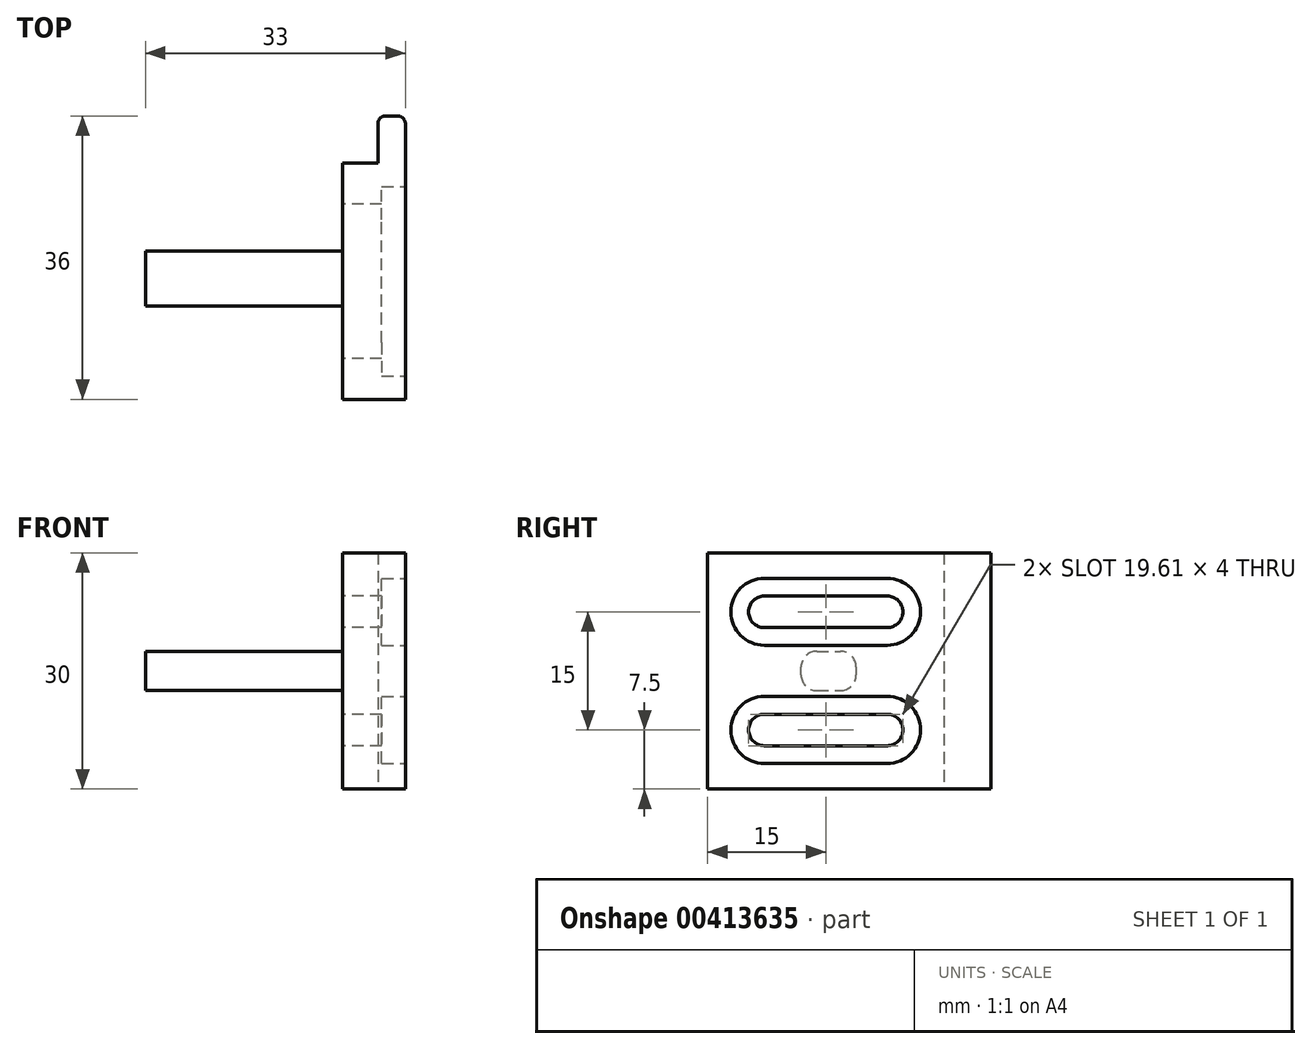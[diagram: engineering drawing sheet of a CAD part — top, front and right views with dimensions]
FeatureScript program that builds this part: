
annotation { "Feature Type Name" : "Feature", "Feature Type Description" : "" }
export const myFeature = defineFeature(function(context is Context, id is Id, definition is map)
    precondition{}
    {
        {
            var Q0;
            Q0=qCreatedBy(makeId("Top.planeOp"),FACE);
            var sketch = newSketch(context, id + "F0", { "sketchPlane" : qUnion([Q0])});
            skLineSegment(sketch, "E0", {"start": v(8, 36) * mm, "end": v(4.5, 36) * mm});
            skLineSegment(sketch, "E1", {"start": v(4.5, 36) * mm, "end": v(4.5, 30) * mm});
            skLineSegment(sketch, "E2", {"start": v(4.5, 30) * mm, "end": v(0, 30) * mm});
            skLineSegment(sketch, "E3", {"start": v(0, 30) * mm, "end": v(0, 0) * mm});
            skLineSegment(sketch, "E4", {"start": v(0, 0) * mm, "end": v(8, 0) * mm});
            skLineSegment(sketch, "E5", {"start": v(8, 0) * mm, "end": v(8, 36) * mm});
            skSolve(sketch);
        }
        {
            var Q0;
            Q0=qSketchRegion(id+"F0",true);
            extrude(context, id + "F1", {"entities" : qUnion([Q0]), "depth" : 30 * mm});
        }
        {
            var Q0;
            Q0=makeQuery(id+"F1.opExtrude","SWEPT_FACE",FACE,{"disambiguationData":[OSD([sQuery(id+"F0.wireOp",EDGE,"E3")])]});
            var sketch = newSketch(context, id + "F2", { "sketchPlane" : qUnion([Q0])});
            skLineSegment(sketch, "E6", {"start": v(-30, 15) * mm, "end": v(0, 15) * mm, "construction": true});
            skLineSegment(sketch, "E7", {"start": v(-7.2, 0) * mm, "end": v(-7.2, 30) * mm, "construction": true});
            skCircle(sketch, "E8", {"center": v(-7.2, 22.5) * mm, "radius": 2 * mm});
            skCircle(sketch, "E9.MirrorC", {"center": v(-7.2, 7.5) * mm, "radius": 2 * mm});
            skLineSegment(sketch, "E10", {"start": v(-15, 30) * mm, "end": v(-15, 0) * mm, "construction": true});
            skLineSegment(sketch, "E11", {"start": v(-7.2, 24.5) * mm, "end": v(-15, 24.5) * mm});
            skLineSegment(sketch, "E12", {"start": v(-7.2, 20.5) * mm, "end": v(-15, 20.5) * mm});
            skLineSegment(sketch, "E13.MirrorCS", {"start": v(-7.2, 5.5) * mm, "end": v(-15, 5.5) * mm});
            skLineSegment(sketch, "E14.MirrorCS", {"start": v(-7.2, 9.5) * mm, "end": v(-15, 9.5) * mm});
            skLineSegment(sketch, "E15.MirrorCS", {"start": v(-22.8, 24.5) * mm, "end": v(-15, 24.5) * mm});
            skLineSegment(sketch, "E16.MirrorCS", {"start": v(-22.8, 20.5) * mm, "end": v(-15, 20.5) * mm});
            skCircle(sketch, "E17.MirrorC", {"center": v(-22.8, 22.5) * mm, "radius": 2 * mm});
            skLineSegment(sketch, "E18.MirrorCS", {"start": v(-22.8, 5.5) * mm, "end": v(-15, 5.5) * mm});
            skLineSegment(sketch, "E19.MirrorCS", {"start": v(-22.8, 9.5) * mm, "end": v(-15, 9.5) * mm});
            skCircle(sketch, "E20.MirrorC", {"center": v(-22.8, 7.5) * mm, "radius": 2 * mm});
            skSolve(sketch);
        }
        {
            var Q0;
            Q0 = qSketchRegion(id + "F2", true);
            var Q1;
            Q1=sQuery(id+"F2.wireOp",EDGE,"E6");
            var Q2;
            Q2=sQuery(id+"F2.wireOp",EDGE,"E7");
            var Q3;
            Q3=sQuery(id+"F2.wireOp",EDGE,"Hv4J3IM8-VowD-CxZo-AhSj-27J0OBbzQMSq");
            var Q4;
            Q4=sQuery(id+"F2.wireOp",EDGE,"gJ8dOzfd-5YLx-k0AR-j59Q-bYQyRviPl2UG");
            extrude(context, id + "F3", {"entities" : qUnion([Q0]), "operationType" : NewBodyOperationType.REMOVE, "surfaceEntities" : qUnion([Q1, Q2, Q3, Q4]), "endBound" : BoundingType.THROUGH_ALL, "oppositeDirection" : true, "depth" : 25 * mm});
        }
        {
            var Q0;
            Q0=makeQuery(id+"F1.opExtrude","SWEPT_EDGE",EDGE,{"disambiguationData":[OSD([sQuery(id+"F0.wireOp",EDGE,"E0"),sQuery(id+"F0.wireOp",EDGE,"E1")])]});
            var Q1;
            Q1=makeQuery(id+"F1.opExtrude","SWEPT_EDGE",EDGE,{"disambiguationData":[OSD([sQuery(id+"F0.wireOp",EDGE,"E0"),sQuery(id+"F0.wireOp",EDGE,"E5")])]});
            fillet(context, id + "F4", {"entities" : qUnion([Q0, Q1]), "radius" : 1 * mm, "tangentPropagation" : true, "allowEdgeOverflow" : false});
        }
        {
            var Q0;
            Q0=makeQuery(id+"F1.opExtrude","SWEPT_FACE",FACE,{"disambiguationData":[OSD([sQuery(id+"F0.wireOp",EDGE,"E5")])]});
            var sketch = newSketch(context, id + "F5", { "sketchPlane" : qUnion([Q0])});
            skCircle(sketch, "E21", {"center": v(7.2, 22.5) * mm, "radius": 4.25 * mm});
            skCircle(sketch, "E22", {"center": v(7.2, 7.5) * mm, "radius": 4.25 * mm});
            skCircle(sketch, "E23", {"center": v(22.8, 22.5) * mm, "radius": 4.25 * mm});
            skCircle(sketch, "E24", {"center": v(22.8, 7.5) * mm, "radius": 4.25 * mm});
            skLineSegment(sketch, "E25", {"start": v(7.2, 26.75) * mm, "end": v(22.8, 26.75) * mm});
            skLineSegment(sketch, "E26", {"start": v(7.2, 18.25) * mm, "end": v(22.8, 18.25) * mm});
            skLineSegment(sketch, "E27", {"start": v(7.2, 11.75) * mm, "end": v(22.8, 11.75) * mm});
            skLineSegment(sketch, "E28", {"start": v(7.2, 3.25) * mm, "end": v(22.8, 3.25) * mm});
            skSolve(sketch);
        }
        {
            var Q0;
            Q0=qSketchRegion(id+"F5",true);
            extrude(context, id + "F6", {"entities" : qUnion([Q0]), "operationType" : NewBodyOperationType.REMOVE, "oppositeDirection" : true, "depth" : 3 * mm});
        }
        {
            var Q0;
            Q0=makeQuery(id+"F1.opExtrude","SWEPT_FACE",FACE,{"disambiguationData":[OSD([sQuery(id+"F0.wireOp",EDGE,"E3")])]});
            var sketch = newSketch(context, id + "F7", { "sketchPlane" : qUnion([Q0])});
            skLineSegment(sketch, "E29.bottom", {"start": v(-11.87, 12.5) * mm, "end": v(-18.85, 12.5) * mm});
            skLineSegment(sketch, "E29.left", {"start": v(-11.87, 12.5) * mm, "end": v(-11.87, 15) * mm});
            skLineSegment(sketch, "E29.right", {"start": v(-18.85, 12.5) * mm, "end": v(-18.85, 15) * mm});
            skLineSegment(sketch, "E30", {"start": v(-7.2, 9.5) * mm, "end": v(-7.2, 20.5) * mm, "construction": true});
            skLineSegment(sketch, "E31", {"start": v(-7.2, 20.5) * mm, "end": v(-7.2, 15) * mm});
            skLineSegment(sketch, "E32", {"start": v(-22.8, 9.5) * mm, "end": v(-22.8, 20.5) * mm, "construction": true});
            skLineSegment(sketch, "E33", {"start": v(-7.2, 15) * mm, "end": v(-22.8, 15) * mm, "construction": true});
            skLineSegment(sketch, "E34.MirrorCS", {"start": v(-18.85, 17.5) * mm, "end": v(-18.85, 15) * mm});
            skLineSegment(sketch, "E35.MirrorCS", {"start": v(-11.87, 17.5) * mm, "end": v(-18.85, 17.5) * mm});
            skLineSegment(sketch, "E36.MirrorCS", {"start": v(-11.87, 17.5) * mm, "end": v(-11.87, 15) * mm});
            skSolve(sketch);
        }
        {
            var Q0;
            Q0 = qSketchRegion(id + "F7", true);
            extrude(context, id + "F8", {"entities" : qUnion([Q0]), "operationType" : NewBodyOperationType.ADD, "depth" : 25 * mm});
        }
        {
            var Q0;
            Q0=makeQuery(id+"F8.opExtrude","CAP_EDGE",EDGE,{"disambiguationData":[OSD([sQuery(id+"F7.wireOp",EDGE,"E29.right"),sQuery(id+"F7.wireOp",EDGE,"E34.MirrorCS")])],"isStart":true});
            var Q1;
            Q1=makeQuery(id+"F8.opExtrude","CAP_EDGE",EDGE,{"disambiguationData":[OSD([sQuery(id+"F7.wireOp",EDGE,"E35.MirrorCS")])],"isStart":true});
            var Q2;
            Q2=makeQuery(id+"F8.opExtrude","CAP_EDGE",EDGE,{"disambiguationData":[OSD([sQuery(id+"F7.wireOp",EDGE,"E29.bottom")])],"isStart":true});
            var Q3;
            Q3=makeQuery(id+"F8.opExtrude","CAP_EDGE",EDGE,{"disambiguationData":[OSD([sQuery(id+"F7.wireOp",EDGE,"E29.left"),sQuery(id+"F7.wireOp",EDGE,"E36.MirrorCS")])],"isStart":true});
            var Q4;
            Q4=makeQuery(id+"F8.opExtrude","SWEPT_EDGE",EDGE,{"disambiguationData":[OSD([sQuery(id+"F7.wireOp",EDGE,"E29.bottom"),sQuery(id+"F7.wireOp",EDGE,"E29.left")])]});
            var Q5;
            Q5=makeQuery(id+"F8.opExtrude","SWEPT_EDGE",EDGE,{"disambiguationData":[OSD([sQuery(id+"F7.wireOp",EDGE,"E35.MirrorCS"),sQuery(id+"F7.wireOp",EDGE,"E36.MirrorCS")])]});
            var Q6;
            Q6=makeQuery(id+"F8.opExtrude","SWEPT_EDGE",EDGE,{"disambiguationData":[OSD([sQuery(id+"F7.wireOp",EDGE,"E29.bottom"),sQuery(id+"F7.wireOp",EDGE,"E29.right")])]});
            var Q7;
            Q7=makeQuery(id+"F8.opExtrude","SWEPT_EDGE",EDGE,{"disambiguationData":[OSD([sQuery(id+"F7.wireOp",EDGE,"E34.MirrorCS"),sQuery(id+"F7.wireOp",EDGE,"E35.MirrorCS")])]});
            fillet(context, id + "F9", {"entities" : qUnion([Q0, Q1, Q2, Q3, Q4, Q5, Q6, Q7]), "radius" : 2 * mm, "tangentPropagation" : true, "allowEdgeOverflow" : false});
        }
    });
